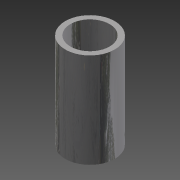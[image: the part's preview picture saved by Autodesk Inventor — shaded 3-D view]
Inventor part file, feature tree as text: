
AUTODESK INVENTOR PART (.ipt)
format: ipt  version: 2015 (Build 190159000, 159)  size: 104,960 bytes
history: native  units: mm
features: sketch x2, other x1, extrude x1, hole x1
ambient origin geometry x8: Origin, YZ Plane, XZ Plane, XY Plane, X Axis, Y Axis, Z Axis, Center Point
bodies: Body1 (feature_tree)
feature tree (5):
  other  "Bryła1"
  extrude  "Wyciągnięcie proste1"  Depth=17.2mm
  hole  "Otwór1"  [1 undecoded]
  sketch  "Szkic1"
  sketch  "Szkic2"
note: 1 required parameter value undecoded (feature->parameter linkage not recoverable at this tier; creation-order binding heuristic only, values carry confidence <= 0.55)
